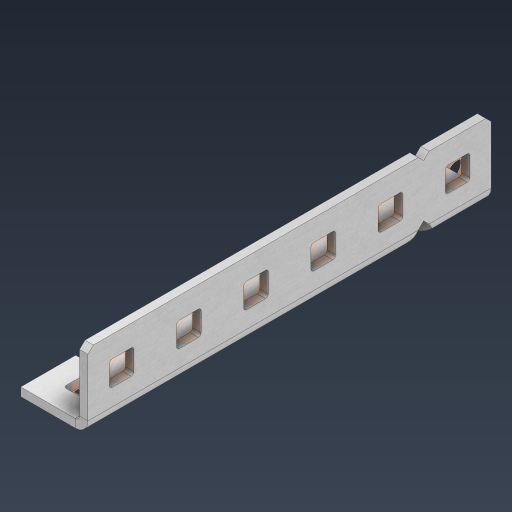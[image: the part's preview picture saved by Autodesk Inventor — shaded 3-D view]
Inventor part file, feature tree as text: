
AUTODESK INVENTOR PART (.ipt)
format: ipt  version: 2024.3 (Build 283343000, 343)  size: 512,000 bytes
history: native  units: in
note: dims shown in document units (in); Inventor stores cm internally (conversion verified against a paired STEP export)
features: other x25, extrude x16, sheet_metal_op x11, pattern_linear x2, mirror x1, chamfer x1, sketch x1
ambient origin geometry x8: Origin, YZ Plane, XZ Plane, XY Plane, X Axis, Y Axis, Z Axis, Center Point
bodies: Solid1 (feature_tree), Body (feature_tree)
feature tree (57):
  sheet_metal_op  "Flanges"
  other  "Flange Pattern Plane"
  other  "Flange Pattern Sketch"
  sheet_metal_op  "Flange Pattern"
  sheet_metal_op  "Body Pattern"
  pattern_linear  "Center Pattern"  Spacing1=3.0in  [1 undecoded]
  other  "Arc Length"
  mirror  "Notch Mirror"
  pattern_linear  "Notch Pattern"  Spacing1=0.0625in  [1 undecoded]
  chamfer  "End Chamfer"
  extrude  "Half Cut"  Depth=0.0625in
  other  "Plate1"
  sketch  "Sketch2"  dims[d0=1.0in d1=3.0in d2=0.0625in d3=0.0625in d4=0.0312in d5=0.125in d6=0.0625in d7=0.5in d8=90.0deg d9=0.0312in d10=0.25in d11=0.0625in d12=0.0625in d16=0.182in d17=0.02in d18=0.0625in d19=0.0in d20=0.25in d21=0.25in d38=2.3622in d40=0.5in d41=0.3937in d43=1.0in d46=0.172in d47=1.0in d48=0.0in d49=0.182in d50=0.02in d51=0.25in d52=0.25in d53=0.0625in d54=0.0in d55=0.172in d56=1.0in d57=0.0in d58=0.25in d60=2.3622in d62=0.5in d63=0.3937in d65=0.5in d85=0.1473in d86=0.1782in d88=0.04in d89=0.0625in d90=0.0in d91=0.04in d92=0.0491in d95=2.5in d96=0.04in d97=0.25in d98=45.0deg d99=0.25in d100=0.5in d101=0.0in d102=2.497in d106=0.182in d107=0.02in d108=0.5in d109=0.5in d110=0.0625in d111=0.0in d112=0.172in d113=0.5in d114=0.0in d117=0.5in d118=0.5in d119=0.5in]
  other  "Plate2"
  sheet_metal_op  "Bend1"
  sheet_metal_op  "Corner1"
  other  "Srf1"
  other  "Srf2"
  other  "Srf91"
  sheet_metal_op  "Body Pattern Sketch"
  other  "Srf92"
  other  "Srf786"
  other  "Srf823"
  other  "Srf824"
  other  "Srf825"
  other  "Srf826"
  other  "Srf856"
  other  "Srf857"
  other  "Srf858"
  other  "Srf859"
  other  "Srf889"
  other  "Srf890"
  other  "Srf891"
  other  "Srf892"
  other  "Srf893"
  sheet_metal_op  "Flange Stamp"
  sheet_metal_op  "Flange Circle"
  sheet_metal_op  "Body Stamp"
  sheet_metal_op  "Body Circle"
  other  "Center Stamp"
  other  "Center Circle"
  sheet_metal_op  "Notch"
  extrude  "ExtrusionSrf2"  Depth=0.5in
  extrude  "ExtrusionSrf92"  Depth=0.5in
  extrude  "ExtrusionSrf823"  Depth=0.0625in
  extrude  "ExtrusionSrf824"  Depth=0.5in TaperAngle=90.0deg
  extrude  "ExtrusionSrf825"  Depth=0.5in
  extrude  "ExtrusionSrf826"  Depth=0.0625in
  extrude  "ExtrusionSrf856"  Depth=0.0625in
  extrude  "ExtrusionSrf857"  Depth=0.182in
  extrude  "ExtrusionSrf858"  Depth=0.02in
  extrude  "ExtrusionSrf859"  Depth=0.0625in
  extrude  "ExtrusionSrf889"  TaperAngle=0.0deg  [1 undecoded]
  extrude  "ExtrusionSrf890"  Depth=0.5in
  extrude  "ExtrusionSrf891"  Depth=0.5in
  extrude  "ExtrusionSrf892"  Depth=0.5in
  extrude  "ExtrusionSrf893"  Depth=0.5in
note: 3 required parameter values undecoded (feature->parameter linkage not recoverable at this tier; creation-order binding heuristic only, values carry confidence <= 0.55)
